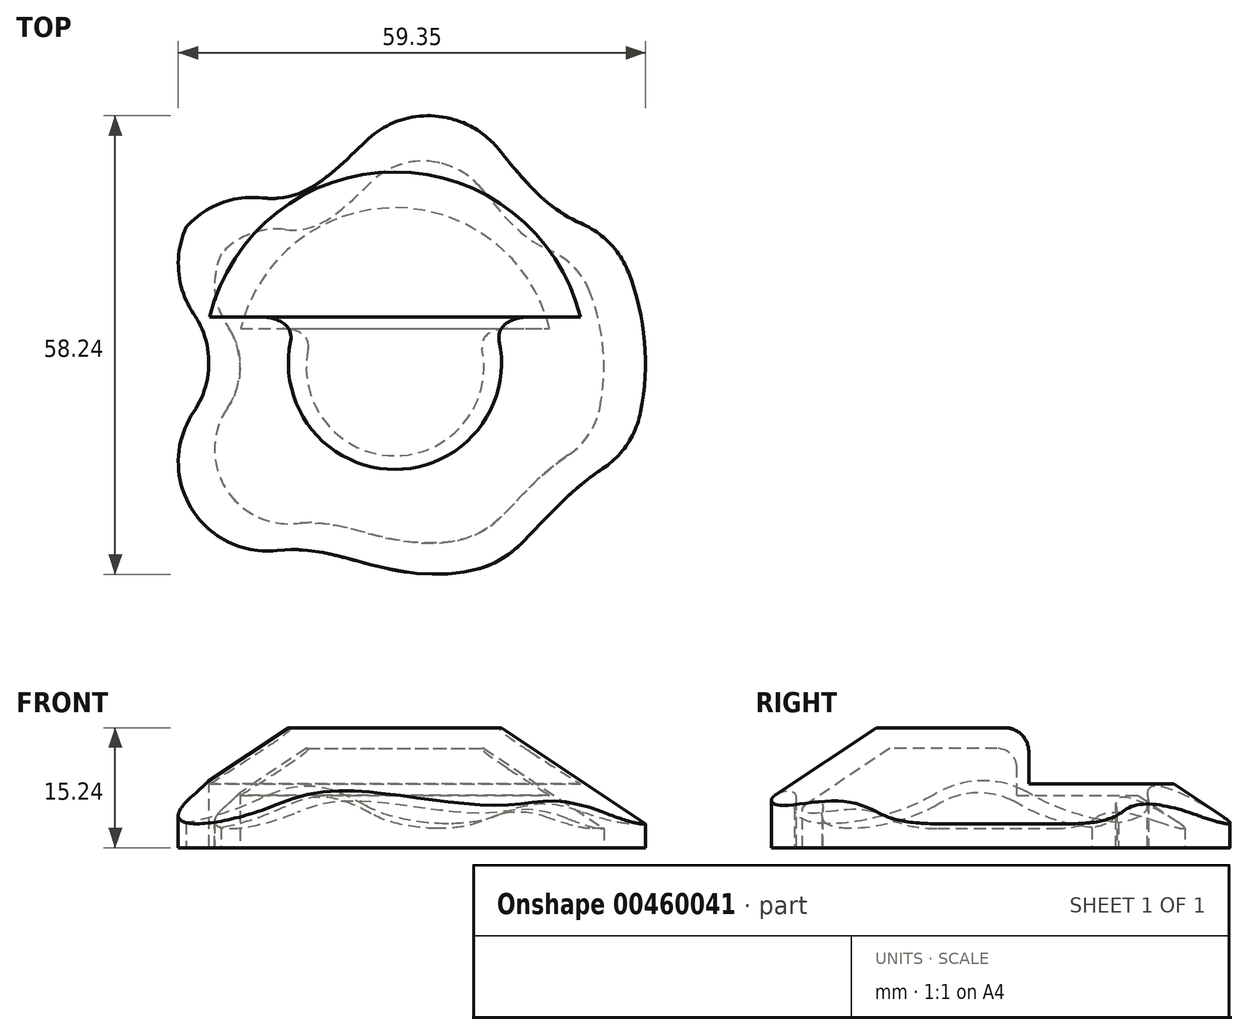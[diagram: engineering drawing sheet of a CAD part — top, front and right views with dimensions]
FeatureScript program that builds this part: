
annotation { "Feature Type Name" : "Feature", "Feature Type Description" : "" }
export const myFeature = defineFeature(function(context is Context, id is Id, definition is map)
    precondition{}
    {
        {
            var Q0;
            Q0=qCreatedBy(makeId("Top.planeOp"),FACE);
            var sketch = newSketch(context, id + "F0", { "sketchPlane" : qUnion([Q0])});
            skCircle(sketch, "E0", {"center": v(-30.84, 0) * mm, "radius": 26.52 * mm});
            skSolve(sketch);
        }
        {
            var Q0;
            Q0=makeQuery(id+"F0.imprint","IMPRINT",FACE,{"disambiguationData":[TD([[makeQuery(id+"F0.imprint","IMPRINT",EDGE,{"derivedFrom":sQuery(id+"F0.wireOp",EDGE,"E0")}),1.0]])]});
            extrude(context, id + "F1", {"entities" : qUnion([Q0]), "depth" : 12.7 * mm, "offsetDistance" : 25.4 * mm});
        }
        {
            var Q0;
            Q0=makeQuery(id+"F1.opExtrude","CAP_EDGE",EDGE,{"disambiguationData":[OSD([sQuery(id+"F0.wireOp",EDGE,"E0")])],"isStart":false});
            chamfer(context, id + "F2", {"entities" : qUnion([Q0]), "chamferType" : ChamferType.TWO_OFFSETS, "width1" : 15.24 * mm, "oppositeDirection" : false, "width2" : 10.16 * mm, "tangentPropagation" : true});
        }
        {
            var Q0;
            Q0=makeQuery(id+"F1.opExtrude","CAP_FACE",FACE,{"disambiguationData":[OSD([sQuery(id+"F0.wireOp",EDGE,"E0")])],"isStart":false});
            var sketch = newSketch(context, id + "F3", { "sketchPlane" : qUnion([Q0])});
            skSolve(sketch);
        }
        {
            var Q0;
            Q0=qCreatedBy(makeId("Right.planeOp"),FACE);
            var sketch = newSketch(context, id + "F4", { "sketchPlane" : qUnion([Q0])});
            skLineSegment(sketch, "E1.bottom", {"start": v(27.4, 19.72) * mm, "end": v(4.86, 19.72) * mm});
            skLineSegment(sketch, "E1.top", {"start": v(27.4, 6.74) * mm, "end": v(4.86, 6.74) * mm});
            skLineSegment(sketch, "E1.left", {"start": v(27.4, 19.72) * mm, "end": v(27.4, 6.74) * mm});
            skLineSegment(sketch, "E1.right", {"start": v(4.86, 19.72) * mm, "end": v(4.86, 6.74) * mm});
            skSolve(sketch);
        }
        {
            var Q0;
            Q0=makeQuery(id+"F4.imprint","IMPRINT",FACE,{"disambiguationData":[TD([[makeQuery(id+"F4.imprint","IMPRINT",EDGE,{"derivedFrom":sQuery(id+"F4.wireOp",EDGE,"E1.bottom")}),1.0]])]});
            extrude(context, id + "F5", {"entities" : qUnion([Q0]), "operationType" : NewBodyOperationType.REMOVE, "oppositeDirection" : true, "depth" : 72.9 * mm, "offsetDistance" : 25.4 * mm});
        }
        {
            var Q0;
            Q0=makeQuery(id+"F5.boolean.opBoolean","INTERSECT",EDGE,{"derivedFrom":[makeQuery(id+"F1.opExtrude","CAP_FACE",FACE,{"disambiguationData":[OSD([sQuery(id+"F0.wireOp",EDGE,"E0")])],"isStart":false}),makeQuery(id+"F5.opExtrude","SWEPT_FACE",FACE,{"disambiguationData":[OSD([sQuery(id+"F4.wireOp",EDGE,"E1.right")])]})]});
            fillet(context, id + "F6", {"entities" : qUnion([Q0]), "radius" : 2.54 * mm, "tangentPropagation" : true, "allowEdgeOverflow" : false});
        }
        {
            var Q0;
            {var subQ0=sQuery(id+"F0.wireOp",EDGE,"E0");Q0=makeQuery(id+"F3.imprint","IMPRINT",FACE,{"disambiguationData":[TD([[makeQuery(id+"F3.imprint","IMPRINT",EDGE,{"derivedFrom":makeQuery(id+"F2.opChamfer","BLEND_EDGE",EDGE,{"blendedFrom":[makeQuery(id+"F1.opExtrude","CAP_EDGE",EDGE,{"disambiguationData":[OSD([subQ0])],"isStart":false}),makeQuery(id+"F1.opExtrude","CAP_FACE",FACE,{"disambiguationData":[OSD([subQ0])],"isStart":false})],"blendedInto":[makeQuery(id+"F1.opExtrude","CAP_FACE",FACE,{"disambiguationData":[OSD([subQ0])],"isStart":false})]})}),1.0]])]});}
            var sketch = newSketch(context, id + "F7", { "sketchPlane" : qUnion([Q0])});
            skPoint(sketch, "E2", {"position": v(-30.7, -2.62) * mm});
            skSolve(sketch);
        }
        {
            var Q0;
            Q0=qCreatedBy(makeId("Top.planeOp"),FACE);
            var sketch = newSketch(context, id + "F8", { "sketchPlane" : qUnion([Q0])});
            skFitSpline(sketch, "E3", {"points": [v(-55.37, 22.95) * mm, v(-40.4, 18.2) * mm, v(-26.77, 28.16) * mm, v(-13.91, 16.36) * mm, v(0, 16.66) * mm, v(-6.34, 40.9) * mm, v(-65.44, 38.9) * mm, v(-55.37, 22.95) * mm]});
            skFitSpline(sketch, "E4", {"points": [v(-51, -23.02) * mm, v(-40.94, -19.79) * mm, v(-30.57, -22) * mm, v(-20.25, -21.15) * mm, v(-12.62, -14.2) * mm, v(-1.06, -9.55) * mm, v(-5.18, -30.16) * mm, v(-53.1, -30.32) * mm, v(-51, -23.02) * mm]});
            skSolve(sketch);
        }
        {
            var Q0;
            Q0 = qSketchRegion(id + "F8", true);
            extrude(context, id + "F9", {"entities" : qUnion([Q0]), "operationType" : NewBodyOperationType.REMOVE, "depth" : 13.97 * mm, "offsetDistance" : 25.4 * mm});
        }
        {
            var Q0;
            Q0=qCreatedBy(makeId("Top.planeOp"),FACE);
            var sketch = newSketch(context, id + "F10", { "sketchPlane" : qUnion([Q0])});
            skCircle(sketch, "E5", {"center": v(-59.74, 0) * mm, "radius": 9.2 * mm});
            skSolve(sketch);
        }
        {
            var Q0;
            Q0 = qSketchRegion(id + "F10", true);
            extrude(context, id + "F11", {"entities" : qUnion([Q0]), "operationType" : NewBodyOperationType.REMOVE, "depth" : 12.45 * mm, "offsetDistance" : 25.4 * mm});
        }
        {
            var Q0;
            Q0=makeQuery(id+"F9.boolean.opBoolean","INTERSECT",EDGE,{"disambiguationData":[OD(0.0)],"derivedFrom":[makeQuery(id+"F1.opExtrude","SWEPT_FACE",FACE,{"disambiguationData":[OSD([sQuery(id+"F0.wireOp",EDGE,"E0")])]}),makeQuery(id+"F9.opExtrude","SWEPT_FACE",FACE,{"disambiguationData":[OSD([sQuery(id+"F8.wireOp",EDGE,"E3")])]})]});
            var Q1;
            Q1=makeQuery(id+"F9.boolean.opBoolean","INTERSECT",EDGE,{"disambiguationData":[OD(1.0)],"derivedFrom":[makeQuery(id+"F1.opExtrude","SWEPT_FACE",FACE,{"disambiguationData":[OSD([sQuery(id+"F0.wireOp",EDGE,"E0")])]}),makeQuery(id+"F9.opExtrude","SWEPT_FACE",FACE,{"disambiguationData":[OSD([sQuery(id+"F8.wireOp",EDGE,"E3")])]})]});
            var Q2;
            Q2=makeQuery(id+"F9.boolean.opBoolean","INTERSECT",EDGE,{"disambiguationData":[OD(2.0)],"derivedFrom":[makeQuery(id+"F1.opExtrude","SWEPT_FACE",FACE,{"disambiguationData":[OSD([sQuery(id+"F0.wireOp",EDGE,"E0")])]}),makeQuery(id+"F9.opExtrude","SWEPT_FACE",FACE,{"disambiguationData":[OSD([sQuery(id+"F8.wireOp",EDGE,"E3")])]})]});
            var Q3;
            Q3=makeQuery(id+"F9.boolean.opBoolean","INTERSECT",EDGE,{"disambiguationData":[OD(0.0)],"derivedFrom":[makeQuery(id+"F1.opExtrude","SWEPT_FACE",FACE,{"disambiguationData":[OSD([sQuery(id+"F0.wireOp",EDGE,"E0")])]}),makeQuery(id+"F9.opExtrude","SWEPT_FACE",FACE,{"disambiguationData":[OSD([sQuery(id+"F8.wireOp",EDGE,"E4")])]})]});
            var Q4;
            Q4=makeQuery(id+"F9.boolean.opBoolean","INTERSECT",EDGE,{"disambiguationData":[OD(1.0)],"derivedFrom":[makeQuery(id+"F1.opExtrude","SWEPT_FACE",FACE,{"disambiguationData":[OSD([sQuery(id+"F0.wireOp",EDGE,"E0")])]}),makeQuery(id+"F9.opExtrude","SWEPT_FACE",FACE,{"disambiguationData":[OSD([sQuery(id+"F8.wireOp",EDGE,"E4")])]})]});
            var Q5;
            Q5=makeQuery(id+"F9.boolean.opBoolean","INTERSECT",EDGE,{"disambiguationData":[OD(3.0)],"derivedFrom":[makeQuery(id+"F1.opExtrude","SWEPT_FACE",FACE,{"disambiguationData":[OSD([sQuery(id+"F0.wireOp",EDGE,"E0")])]}),makeQuery(id+"F9.opExtrude","SWEPT_FACE",FACE,{"disambiguationData":[OSD([sQuery(id+"F8.wireOp",EDGE,"E3")])]})]});
            var Q6;
            {var subQ0=sQuery(id+"F0.wireOp",EDGE,"E0");Q6=makeQuery(id+"F11.boolean.opBoolean","INTERSECT",EDGE,{"disambiguationData":[OD(1.0)],"derivedFrom":[makeQuery(id+"F9.boolean.opBoolean","SPLIT",FACE,{"disambiguationData":[TD([makeQuery(id+"F1.opExtrude","CAP_FACE",FACE,{"disambiguationData":[OSD([subQ0])],"isStart":true}),makeQuery(id+"F2.opChamfer","BLEND_FACE",FACE,{"disambiguationData":[OSD([subQ0])]}),makeQuery(id+"F9.opExtrude","SWEPT_FACE",FACE,{"disambiguationData":[OSD([sQuery(id+"F8.wireOp",EDGE,"E3")])]}),makeQuery(id+"F9.opExtrude","SWEPT_FACE",FACE,{"disambiguationData":[OSD([sQuery(id+"F8.wireOp",EDGE,"E4")])]})]),OD(0.0)],"derivedFrom":makeQuery(id+"F1.opExtrude","SWEPT_FACE",FACE,{"disambiguationData":[OSD([subQ0])]})}),makeQuery(id+"F11.opExtrude","SWEPT_FACE",FACE,{"disambiguationData":[OSD([sQuery(id+"F10.wireOp",EDGE,"E5")])]})]});}
            var Q7;
            {var subQ0=sQuery(id+"F0.wireOp",EDGE,"E0");Q7=makeQuery(id+"F11.boolean.opBoolean","INTERSECT",EDGE,{"disambiguationData":[OD(0.0)],"derivedFrom":[makeQuery(id+"F9.boolean.opBoolean","SPLIT",FACE,{"disambiguationData":[TD([makeQuery(id+"F1.opExtrude","CAP_FACE",FACE,{"disambiguationData":[OSD([subQ0])],"isStart":true}),makeQuery(id+"F2.opChamfer","BLEND_FACE",FACE,{"disambiguationData":[OSD([subQ0])]}),makeQuery(id+"F9.opExtrude","SWEPT_FACE",FACE,{"disambiguationData":[OSD([sQuery(id+"F8.wireOp",EDGE,"E3")])]}),makeQuery(id+"F9.opExtrude","SWEPT_FACE",FACE,{"disambiguationData":[OSD([sQuery(id+"F8.wireOp",EDGE,"E4")])]})]),OD(0.0)],"derivedFrom":makeQuery(id+"F1.opExtrude","SWEPT_FACE",FACE,{"disambiguationData":[OSD([subQ0])]})}),makeQuery(id+"F11.opExtrude","SWEPT_FACE",FACE,{"disambiguationData":[OSD([sQuery(id+"F10.wireOp",EDGE,"E5")])]})]});}
            fillet(context, id + "F12", {"entities" : qUnion([Q0, Q1, Q2, Q3, Q4, Q5, Q6, Q7]), "radius" : 9.42 * mm, "tangentPropagation" : true, "allowEdgeOverflow" : false});
        }
        {
            var Q0;
            Q0=makeQuery(id+"F1.opExtrude","SWEPT_BODY",BODY,{"disambiguationData":[OSD([sQuery(id+"F0.wireOp",EDGE,"E0")])]});
            var Q1;
            Q1=sQuery(id+"F7.wireOp",VERTEX,"E2");
            transform(context, id + "F13", {"entities" : qUnion([Q0]), "transformType" : TransformType.SCALE_UNIFORMLY, "scale" : 1.2, "scalePoint" : qUnion([Q1]), "makeCopy" : true});
        }
        {
            var Q0;
            Q0=makeQuery(id+"F13.opPattern","COPY",BODY,{"derivedFrom":makeQuery(id+"F1.opExtrude","SWEPT_BODY",BODY,{"disambiguationData":[OSD([sQuery(id+"F0.wireOp",EDGE,"E0")])]}),"instanceName":"1"});
            transform(context, id + "F14", {"entities" : qUnion([Q0]), "transformType" : TransformType.TRANSLATION_3D, "dx" : 0 * mm, "dy" : 0 * mm, "dz" : 2.64 * mm, "makeCopy" : false});
        }
        {
            var Q0;
            Q0=makeQuery(id+"F1.opExtrude","SWEPT_BODY",BODY,{"disambiguationData":[OSD([sQuery(id+"F0.wireOp",EDGE,"E0")])]});
            var Q1;
            Q1=makeQuery(id+"F13.opPattern","COPY",BODY,{"derivedFrom":makeQuery(id+"F1.opExtrude","SWEPT_BODY",BODY,{"disambiguationData":[OSD([sQuery(id+"F0.wireOp",EDGE,"E0")])]}),"instanceName":"1"});
            booleanBodies(context, id + "F15", {"operationType" : BooleanOperationType.SUBTRACTION, "tools" : qUnion([Q0]), "targets" : qUnion([Q1])});
        }
    });
